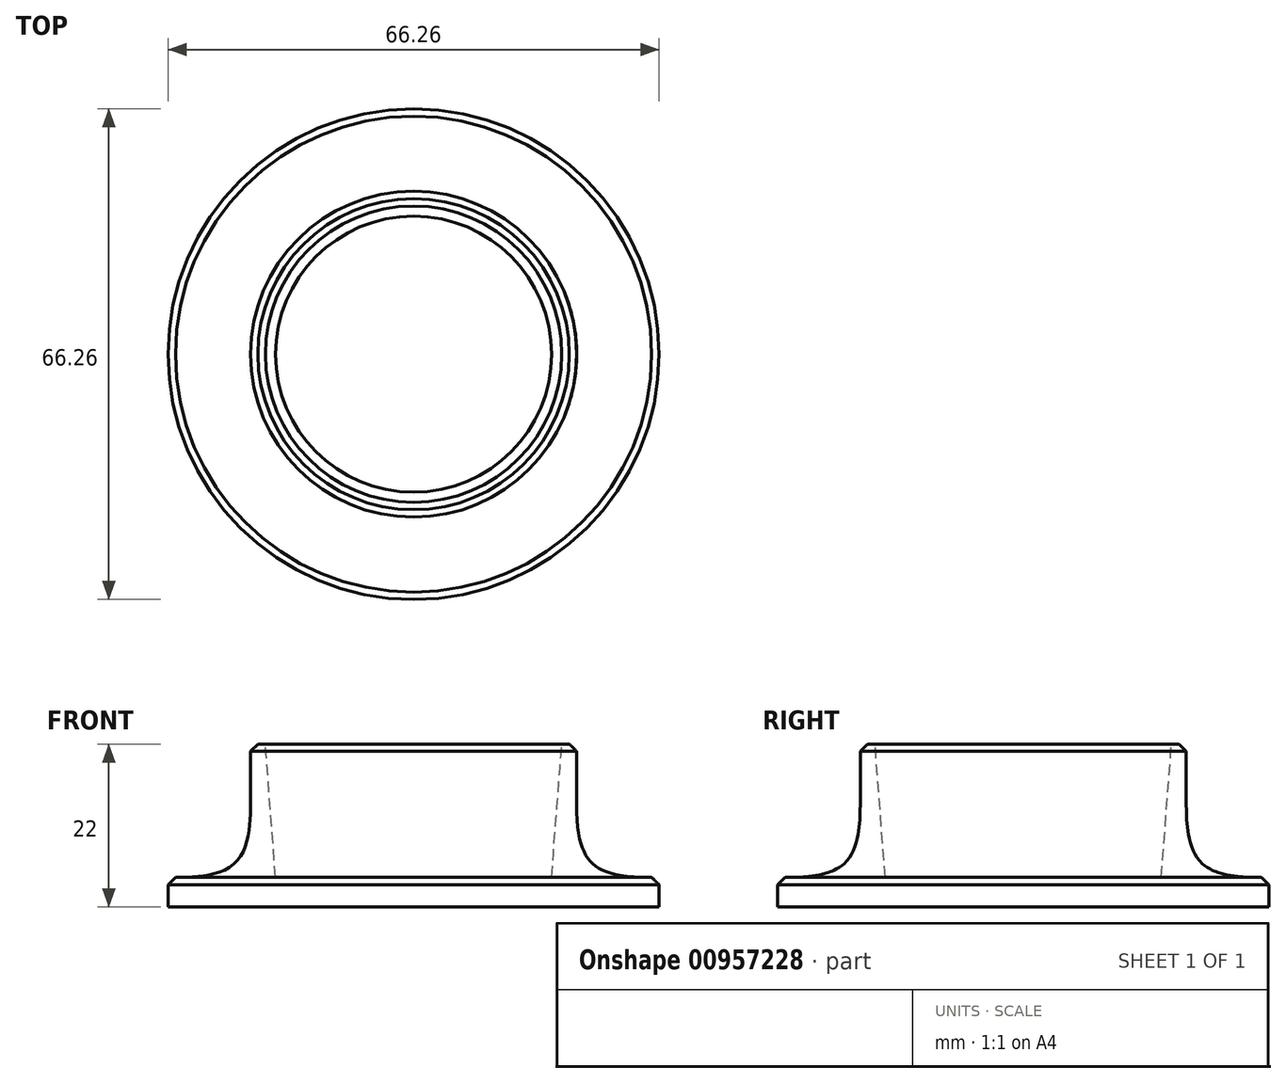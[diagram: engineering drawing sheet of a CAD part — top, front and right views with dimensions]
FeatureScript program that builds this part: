
annotation { "Feature Type Name" : "Feature", "Feature Type Description" : "" }
export const myFeature = defineFeature(function(context is Context, id is Id, definition is map)
    precondition{}
    {
        {
            var Q0;
            Q0=qCreatedBy(makeId("Top.planeOp"),FACE);
            var sketch = newSketch(context, id + "F0", { "sketchPlane" : qUnion([Q0])});
            skCircle(sketch, "E0", {"center": v(0, 0) * mm, "radius": 18.62 * mm});
            skSolve(sketch);
        }
        {
            var Q0;
            Q0=qCreatedBy(makeId("Top.planeOp"),FACE);
            var sketch = newSketch(context, id + "F1", { "sketchPlane" : qUnion([Q0])});
            skCircle(sketch, "E1", {"center": v(0, 0) * mm, "radius": 20.62 * mm});
            skSolve(sketch);
        }
        {
            var Q0;
            Q0 = qSketchRegion(id + "F1", true);
            extrude(context, id + "F2", {"entities" : qUnion([Q0]), "depth" : 20 * mm, "offsetDistance" : 25 * mm});
        }
        {
            var Q0;
            Q0=makeQuery(id+"F2.opExtrude","CAP_FACE",FACE,{"disambiguationData":[OSD([sQuery(id+"F1.wireOp",EDGE,"E1")])],"isStart":false});
            var sketch = newSketch(context, id + "F3", { "sketchPlane" : qUnion([Q0])});
            skCircle(sketch, "E2", {"center": v(0, 0) * mm, "radius": 18.62 * mm});
            skSolve(sketch);
        }
        {
            var Q0;
            Q0=qCreatedBy(makeId("Top.planeOp"),FACE);
            var sketch = newSketch(context, id + "F4", { "sketchPlane" : qUnion([Q0])});
            skCircle(sketch, "E3", {"center": v(0, 0) * mm, "radius": 33.12 * mm});
            skCircle(sketch, "E4", {"center": v(0, 0) * mm, "radius": 20.62 * mm});
            skSolve(sketch);
        }
        {
            var Q0;
            Q0=makeQuery(id+"F4.imprint","IMPRINT",FACE,{"disambiguationData":[TD([[makeQuery(id+"F4.imprint","IMPRINT",EDGE,{"derivedFrom":sQuery(id+"F4.wireOp",EDGE,"E3")}),1.0]])]});
            extrude(context, id + "F5", {"entities" : qUnion([Q0]), "operationType" : NewBodyOperationType.ADD, "depth" : 2 * mm, "offsetDistance" : 25 * mm});
        }
        {
            var Q0;
            Q0=makeQuery(id+"F0.imprint","IMPRINT",FACE,{"disambiguationData":[TD([[makeQuery(id+"F0.imprint","IMPRINT",EDGE,{"derivedFrom":sQuery(id+"F0.wireOp",EDGE,"E0")}),1.0]])]});
            var sketch = newSketch(context, id + "F6", { "sketchPlane" : qUnion([Q0])});
            skCircle(sketch, "E5", {"center": v(0, 0) * mm, "radius": 33.12 * mm});
            skSolve(sketch);
        }
        {
            var Q0;
            Q0 = qSketchRegion(id + "F6", true);
            extrude(context, id + "F7", {"entities" : qUnion([Q0]), "operationType" : NewBodyOperationType.ADD, "oppositeDirection" : true, "depth" : 2 * mm, "offsetDistance" : 25 * mm});
        }
        {
            var Q0;
            Q0=makeQuery(id+"F3.imprint","IMPRINT",FACE,{"disambiguationData":[TD([[makeQuery(id+"F3.imprint","IMPRINT",EDGE,{"derivedFrom":sQuery(id+"F3.wireOp",EDGE,"E2")}),1.0]])]});
            var sketch = newSketch(context, id + "F8", { "sketchPlane" : qUnion([Q0])});
            skCircle(sketch, "E6", {"center": v(0, 0) * mm, "radius": 22 * mm});
            skSolve(sketch);
        }
        {
            var Q0;
            Q0=makeQuery(id+"F8.imprint","IMPRINT",FACE,{"disambiguationData":[TD([[makeQuery(id+"F8.imprint","IMPRINT",EDGE,{"derivedFrom":sQuery(id+"F8.wireOp",EDGE,"E6")}),1.0]])]});
            extrude(context, id + "F9", {"entities" : qUnion([Q0]), "operationType" : NewBodyOperationType.ADD, "endBound" : BoundingType.UP_TO_NEXT, "oppositeDirection" : true, "depth" : 10 * mm, "offsetDistance" : 25 * mm});
        }
        {
            var Q0;
            Q0=makeQuery(id+"F3.imprint","IMPRINT",FACE,{"disambiguationData":[TD([[makeQuery(id+"F3.imprint","IMPRINT",EDGE,{"derivedFrom":sQuery(id+"F3.wireOp",EDGE,"E2")}),1.0]])]});
            var sketch = newSketch(context, id + "F10", { "sketchPlane" : qUnion([Q0])});
            skCircle(sketch, "E7", {"center": v(0, 0) * mm, "radius": 20 * mm});
            skSolve(sketch);
        }
        {
            var Q0;
            Q0 = qSketchRegion(id + "F10", true);
            extrude(context, id + "F11", {"entities" : qUnion([Q0]), "operationType" : NewBodyOperationType.REMOVE, "oppositeDirection" : true, "depth" : 18 * mm, "offsetDistance" : 25 * mm});
        }
        {
            var Q0;
            Q0=makeQuery(id+"F11.boolean.opBoolean","COPY",EDGE,{"derivedFrom":makeQuery(id+"F11.opExtrude","CAP_EDGE",EDGE,{"disambiguationData":[OSD([sQuery(id+"F10.wireOp",EDGE,"E7")])],"isStart":false})});
            chamfer(context, id + "F12", {"entities" : qUnion([Q0]), "chamferType" : ChamferType.TWO_OFFSETS, "width1" : 1.38 * mm, "oppositeDirection" : false, "width2" : 18 * mm, "tangentPropagation" : true});
        }
        {
            var Q0;
            Q0=makeQuery(id+"F9.opExtrude","CAP_EDGE",EDGE,{"disambiguationData":[OSD([sQuery(id+"F8.wireOp",EDGE,"E6")])],"isStart":true});
            chamfer(context, id + "F13", {"entities" : qUnion([Q0]), "width" : 1 * mm, "tangentPropagation" : true});
        }
        {
            var Q0;
            Q0=makeQuery(id+"F9.boolean.opBoolean","INTERSECT",EDGE,{"derivedFrom":[makeQuery(id+"F5.opExtrude","CAP_FACE",FACE,{"disambiguationData":[OSD([sQuery(id+"F4.wireOp",EDGE,"E3"),sQuery(id+"F4.wireOp",EDGE,"E4")])],"isStart":false}),makeQuery(id+"F9.opExtrude","SWEPT_FACE",FACE,{"disambiguationData":[OSD([sQuery(id+"F8.wireOp",EDGE,"E6")])]})]});
            fillet(context, id + "F14", {"entities" : qUnion([Q0]), "radius" : 10 * mm, "tangentPropagation" : true, "rho" : 0.6, "crossSection" : FilletCrossSection.CONIC, "allowEdgeOverflow" : false});
        }
        {
            var Q0;
            Q0=makeQuery(id+"F5.opExtrude","CAP_EDGE",EDGE,{"disambiguationData":[OSD([sQuery(id+"F4.wireOp",EDGE,"E3")])],"isStart":false});
            chamfer(context, id + "F15", {"entities" : qUnion([Q0]), "width" : 1 * mm, "tangentPropagation" : true});
        }
    });
